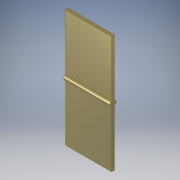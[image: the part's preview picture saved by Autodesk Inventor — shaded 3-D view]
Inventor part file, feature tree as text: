
AUTODESK INVENTOR PART (.ipt)
format: ipt  version: 2018 (Build 220112000, 112)  size: 102,912 bytes
history: native  units: in
note: dims shown in document units (in); Inventor stores cm internally (conversion verified against a paired STEP export)
features: extrude x1, sketch x1
ambient origin geometry x8: Origin, YZ Plane, XZ Plane, XY Plane, X Axis, Y Axis, Z Axis, Center Point
bodies: Solid1 (feature_tree)
feature tree (2):
  extrude  "Extrusion1"  Depth=0.0787in
  sketch  "Sketch1"  dims[d0=0.1575in d1=0.0787in d2=0.0394in d3=1.1811in d4=0.0in]
